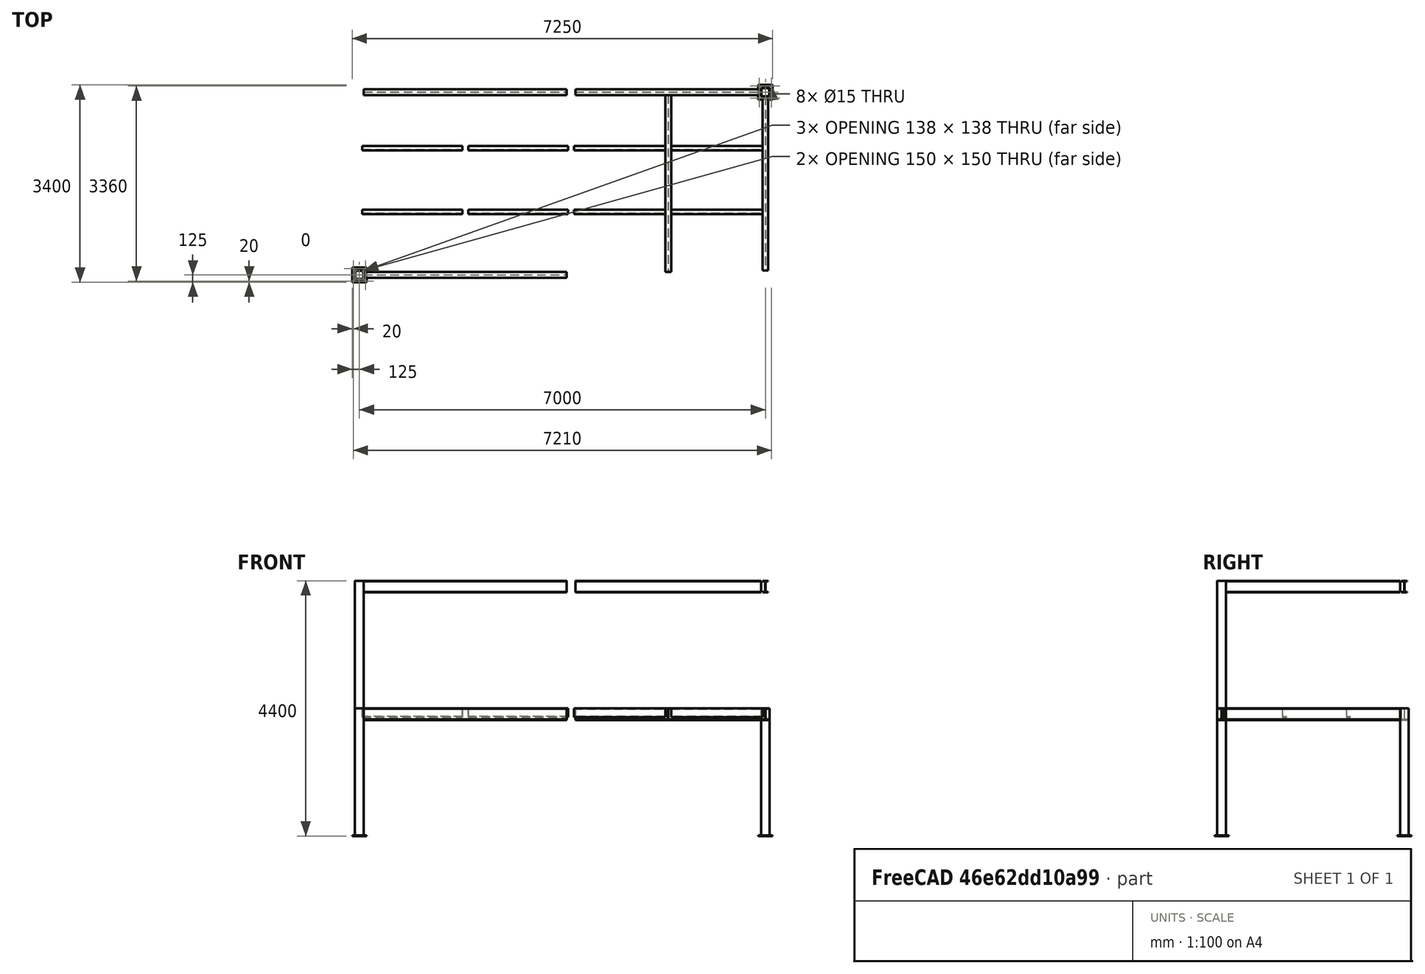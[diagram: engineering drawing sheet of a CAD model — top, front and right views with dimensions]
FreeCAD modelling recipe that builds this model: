
FCSTD DOCUMENT  (FreeCAD 0.20R29177 +426 (Git))
Label: steelframe2
License: All rights reserved
LicenseURL: http://en.wikipedia.org/wiki/All_rights_reserved
objects: App::FeaturePython×181, Part::FeaturePython×121, App::Link×12, Part::Extrusion×1, Part::MultiFuse×1
note: 122 computed .brp shape members not serialized (recipe doc carries the construction recipe); baked Part::Feature solids carry a one-line shape summary decoded from their .brp

FEATURE [Part::FeaturePython] BasePlate  # WARN: FeaturePython — macro-defined, semantics opaque (R4)
  B = 250
  D = 15
  H = 250
  b1 = 20
  h1 = 20
  sface = 0
FEATURE [Part::FeaturePython] SquarePipe_SS  # WARN: FeaturePython — macro-defined, semantics opaque (R4)
  L = 2200
  Solid = true
  size = 43
  standard = SS
FEATURE [Part::Extrusion] Extrude
  Base = -> BasePlate
  Dir = (0,0,1)
  DirMode = 2
  FaceMakerClass = Part::FaceMakerBullseye
  LengthFwd = 9
  LengthRev = 0
  Solid = true
  Symmetric = false
FEATURE [Part::MultiFuse] Fusion  label="Square-steel pipe"
  Placement = pos=(1.063e-12,6.983e-12,237) rot=(0,0,1;0rad)
  Shapes = -> [SquarePipe_SS,Extrude]
FEATURE [Part::FeaturePython] H200x100x5_5_8  label="H_thin"  # WARN: FeaturePython — macro-defined, semantics opaque (R4)
  L = 3000
  Placement = pos=(1.1069e-12,3075,2337) rot=(1,0,0;1.5708rad)
  Solid = true
  size = 5
  standard = SS_Thin
FEATURE [App::Link] Link  label="Square-steel pipe001"
  LinkPlacement = pos=(3650,2.14375e-11,237) rot=(0,0,1;0rad)
  LinkedObject = -> Fusion
  Placement = pos=(3650,2.14375e-11,237) rot=(0,0,1;0rad)
FEATURE [Part::FeaturePython] H200x100x5_5_009  label="H_thin001"  # WARN: FeaturePython — macro-defined, semantics opaque (R4)
  L = 3500
  Placement = pos=(75,7.6577e-12,2337) rot=(0.57735,0.57735,0.57735;2.0944rad)
  Solid = true
  size = 5
  standard = SS_Thin
  expr: L = 3500
FEATURE [App::Link] Link001  label="Square-steel pipe002"
  LinkPlacement = pos=(1.0657e-12,3150,237) rot=(0,0,1;0rad)
  LinkedObject = -> Fusion
  Placement = pos=(1.0657e-12,3150,237) rot=(0,0,1;0rad)
FEATURE [Part::FeaturePython] H200x100x5_5_010  label="H_thin002"  # WARN: FeaturePython — macro-defined, semantics opaque (R4)
  L = 3200
  Placement = pos=(3725,-3.5035e-12,2337) rot=(0.57735,0.57735,0.57735;2.0944rad)
  Solid = true
  size = 5
  standard = SS_Thin
FEATURE [App::Link] Link002  label="Square-steel pipe003"
  LinkPlacement = pos=(7000,-1.45687e-10,237) rot=(0,0,1;0rad)
  LinkedObject = -> Link
  Placement = pos=(7000,-1.45687e-10,237) rot=(0,0,1;0rad)
FEATURE [App::Link] Link003  label="H_thin003"
  LinkPlacement = pos=(75,3150,2337) rot=(0.57735,0.57735,0.57735;2.0944rad)
  LinkedObject = -> H200x100x5_5_009
  Placement = pos=(75,3150,2337) rot=(0.57735,0.57735,0.57735;2.0944rad)
FEATURE [App::Link] Link004  label="Square-steel pipe004"
  LinkPlacement = pos=(3650,3150,237) rot=(0,0,1;0rad)
  LinkedObject = -> Link
  Placement = pos=(3650,3150,237) rot=(0,0,1;0rad)
FEATURE [Part::FeaturePython] Clone  label="H_thin004"  # Draft clone (typed FeaturePython)
  AttacherType = Attacher::AttachEngine3D
  Fuse = false
  Objects = -> [H200x100x5_5_8]
  Placement = pos=(3650,3075,2337) rot=(1,0,0;1.5708rad)
  Scale = (1,1,1)
FEATURE [Part::FeaturePython] Clone001  label="H_thin005"  # Draft clone (typed FeaturePython)
  AttacherType = Attacher::AttachEngine3D
  Fuse = false
  Objects = -> [H200x100x5_5_010]
  Placement = pos=(3725,3150,2337) rot=(0.57735,0.57735,0.57735;2.0944rad)
  Scale = (1,1,1)
FEATURE [Part::FeaturePython] Clone002  label="Square-steel pipe005"  # Draft clone (typed FeaturePython)
  AttacherType = Attacher::AttachEngine3D
  Fuse = false
  Objects = -> [Link002]
  Placement = pos=(7000,3150,237) rot=(0,0,1;0rad)
  Scale = (1,1,1)
FEATURE [Part::FeaturePython] Clone003  label="H_thin006"  # Draft clone (typed FeaturePython)
  AttacherType = Attacher::AttachEngine3D
  Fuse = false
  Objects = -> [Clone]
  Placement = pos=(7000,3075,2337) rot=(1,0,0;1.5708rad)
  Scale = (1,1,1)
FEATURE [Part::FeaturePython] H200x100x5_5_011  label="H_thin007"  # WARN: FeaturePython — macro-defined, semantics opaque (R4)
  L = 3050
  Placement = pos=(1825,3100,2337) rot=(1,0,0;1.5708rad)
  Solid = true
  size = 5
  standard = SS_Thin
FEATURE [Part::FeaturePython] Clone004  label="H_thin008"  # Draft clone (typed FeaturePython)
  AttacherType = Attacher::AttachEngine3D
  Fuse = false
  Objects = -> [H200x100x5_5_011]
  Placement = pos=(5325,3100,2337) rot=(1,0,0;1.5708rad)
  Scale = (1,1,1)
FEATURE [Part::FeaturePython] C150x75x007  label="Channel001"  # WARN: FeaturePython — macro-defined, semantics opaque (R4)
  L = 1575
  Placement = pos=(3700,1086.25,2362) rot=(0.57735,0.57735,0.57735;2.0944rad)
  Solid = true
  size = 3
  standard = SS
FEATURE [Part::FeaturePython] C150x75x008  label="Channel002"  # WARN: FeaturePython — macro-defined, semantics opaque (R4)
  L = 1725
  Placement = pos=(50.0219,1086.25,2362) rot=(0.57735,0.57735,0.57735;2.0944rad)
  Solid = true
  size = 3
  standard = SS
FEATURE [Part::FeaturePython] SquarePipe_SS001  label="SQ_Pipe"  # WARN: FeaturePython — macro-defined, semantics opaque (R4)
  L = 2200
  Placement = pos=(1.063e-12,2.583e-12,2437) rot=(0,0,1;2e-06rad)
  Solid = true
  size = 43
  standard = SS
FEATURE [App::Link] Link005  label="SQ_Pipe001"
  LinkPlacement = pos=(1.0817e-12,3150,2437) rot=(0,0,1;0rad)
  LinkedObject = -> SquarePipe_SS001
  Placement = pos=(1.0817e-12,3150,2437) rot=(0,0,1;0rad)
FEATURE [App::Link] Link006  label="SQ_Pipe002"
  LinkPlacement = pos=(3650,-1.32887e-11,2437) rot=(0,0,1;0rad)
  LinkedObject = -> SquarePipe_SS001
  Placement = pos=(3650,-1.32887e-11,2437) rot=(0,0,1;0rad)
FEATURE [App::Link] Link007  label="SQ_Pipe003"
  LinkPlacement = pos=(3650,3150,2437) rot=(0,0,1;0rad)
  LinkedObject = -> Link006
  Placement = pos=(3650,3150,2437) rot=(0,0,1;0rad)
FEATURE [App::Link] Link008  label="SQ_Pipe004"
  LinkPlacement = pos=(7000,2.22996e-10,2437) rot=(0,0,1;0rad)
  LinkedObject = -> Link007
  Placement = pos=(7000,2.22996e-10,2437) rot=(0,0,1;0rad)
FEATURE [App::Link] Link009  label="SQ_Pipe005"
  LinkPlacement = pos=(7000,3150,2437) rot=(0,0,1;0rad)
  LinkedObject = -> Link008
  Placement = pos=(7000,3150,2437) rot=(0,0,1;0rad)
FEATURE [App::Link] Link010  label="H_thin009"
  LinkPlacement = pos=(75,0.000150522,4537) rot=(0.577351,-0.57735,0.57735;4.18879rad)
  LinkedObject = -> H200x100x5_5_009
  Placement = pos=(75,0.000150522,4537) rot=(0.577351,-0.57735,0.57735;4.18879rad)
FEATURE [App::Link] Link011  label="H_thin010"
  LinkPlacement = pos=(-0.000150522,75,4537) rot=(-1,-1e-06,1e-06;1.5708rad)
  LinkedObject = -> H200x100x5_5_8
  Placement = pos=(-0.000150522,75,4537) rot=(-1,-1e-06,1e-06;1.5708rad)
FEATURE [Part::FeaturePython] Clone005  label="H_thin011"  # Draft clone (typed FeaturePython)
  AttacherType = Attacher::AttachEngine3D
  Fuse = false
  Objects = -> [H200x100x5_5_010]
  Placement = pos=(3725,-1.20515e-10,4537) rot=(0.57735,0.57735,0.57735;2.0944rad)
  Scale = (1,1,1)
FEATURE [Part::FeaturePython] Clone006  label="H_thin012"  # Draft clone (typed FeaturePython)
  AttacherType = Attacher::AttachEngine3D
  Fuse = false
  Objects = -> [Link011]
  Placement = pos=(3650,75,4537) rot=(-1,0,0;1.5708rad)
  Scale = (1,1,1)
FEATURE [Part::FeaturePython] Clone007  label="H_thin013"  # Draft clone (typed FeaturePython)
  AttacherType = Attacher::AttachEngine3D
  Fuse = false
  Objects = -> [Clone006]
  Placement = pos=(7000,75,4537) rot=(-1,0,0;1.5708rad)
  Scale = (1,1,1)
FEATURE [Part::FeaturePython] Clone008  label="H_thin014"  # Draft clone (typed FeaturePython)
  AttacherType = Attacher::AttachEngine3D
  Fuse = false
  Objects = -> [Link010]
  Placement = pos=(75,3150,4537) rot=(-0.57735,0.57735,-0.57735;2.0944rad)
  Scale = (1,1,1)
FEATURE [Part::FeaturePython] Clone009  label="H_thin015"  # Draft clone (typed FeaturePython)
  AttacherType = Attacher::AttachEngine3D
  Fuse = false
  Objects = -> [Clone005]
  Placement = pos=(3725,3150,4537) rot=(0.57735,0.57735,0.57735;2.0944rad)
  Scale = (1,1,1)
FEATURE [Part::FeaturePython] Array002  # Draft array (typed FeaturePython)
  Angle = 360
  ArrayType = 0
  Axis = (0,0,1)
  Base = -> C150x75x007
  Center = (0,0,0)
  Fuse = false
  IntervalAxis = (0,0,0)
  IntervalX = (1675,0,0)
  IntervalY = (0,1100,0)
  IntervalZ = (0,0,50)
  NumberCircles = 3
  NumberPolar = 5
  NumberX = 2
  NumberY = 2
  NumberZ = 1
  RadialDistance = 50
  Symmetry = 1
  TangentialDistance = 25
FEATURE [Part::FeaturePython] Array  # Draft array (typed FeaturePython)
  Angle = 360
  ArrayType = 0
  Axis = (0,0,1)
  Base = -> C150x75x008
  Center = (0,0,0)
  Fuse = false
  IntervalAxis = (0,0,0)
  IntervalX = (1826,0,0)
  IntervalY = (0,1100,0)
  IntervalZ = (0,0,50)
  NumberCircles = 3
  NumberPolar = 5
  NumberX = 2
  NumberY = 2
  NumberZ = 1
  RadialDistance = 50
  Symmetry = 1
  TangentialDistance = 25
FEATURE [Part::FeaturePython] Parts  # WARN: FeaturePython — macro-defined, semantics opaque (R4)
  Group = -> [Fusion,H200x100x5_5_8,Link,H200x100x5_5_009,Link001,H200x100x5_5_010,Link002,Link003,Link004,Clone,Clone001,Clone002,Clone003,H200x100x5_5_011,Clone004,C150x75x007,C150x75x008,SquarePipe_SS001,Link005,Link006,Link007,Link008,Link009,Link010,Link011,Clone005,Clone006,Clone007,Clone008,Clone009,Array002,Array]
  GroupMode = 0
FEATURE [Part::FeaturePython] Assembly  # WARN: FeaturePython — macro-defined, semantics opaque (R4)
  AutoRelax = true
  BuildShape = 0
  Freeze = false
  Group = -> [Constraints,Elements,Parts]
  Verbose = false
  _SolverType = 1
  _Version = 1
FEATURE [App::FeaturePython] Constraints  # WARN: FeaturePython — macro-defined, semantics opaque (R4)
  Group = -> [Constraint,Constraint001,Constraint002,Constraint003,Constraint004,Constraint005,Constraint006,Constraint007,Constraint008,Constraint009,Constraint010,Constraint011,Constraint012,Constraint013,Constraint014,Constraint015,Constraint016,Constraint017,Constraint018,Constraint019,Constraint020,Constraint021,Constraint022,Constraint023,Constraint024,Constraint025,Constraint026,Constraint027,+32 more]
  _Version = 1
FEATURE [App::FeaturePython] Elements  # WARN: FeaturePython — macro-defined, semantics opaque (R4)
  Group = -> [_Element,_Element001,_Element002,_Element003,_Element004,_Element005,_Element006,_Element007,_Element008,_Element009,_Element010,_Element011,_Element012,_Element013,_Element014,_Element015,_Element016,_Element017,_Element018,_Element019,_Element020,_Element021,_Element022,_Element023,_Element024,_Element025,_Element026,_Element027,_Element028,_Element029,_Element030,_Element031,_Element032,+65 more]
FEATURE [App::FeaturePython] Constraint  label="PlaneCoincident"  # WARN: FeaturePython — macro-defined, semantics opaque (R4)
  Angle = 0
  AnglePitch = 0
  AngleRoll = 0
  Cascade = false
  Disabled = false
  Group = -> [ElementLink,ElementLink001]
  LockAngle = false
  Multiply = false
  OffsetX = 0
  OffsetY = 0
  _ConstraintType = 35
  _Parent = -> Constraints
FEATURE [App::FeaturePython] ElementLink  label="_Element"  # link proxy (typed FeaturePython)
  LinkTransform = true
  LinkedObject = -> _Element
  _Parent = -> Constraint
FEATURE [Part::FeaturePython] _Element  # link proxy (typed FeaturePython)
  Detach = false
  LinkTransform = true
  LinkedObject = -> SquarePipe_SS001 [Face17]
  _Parent = -> Elements
FEATURE [App::FeaturePython] ElementLink001  label="_Element001"  # link proxy (typed FeaturePython)
  LinkTransform = true
  LinkedObject = -> _Element001
  _Parent = -> Constraint
FEATURE [Part::FeaturePython] _Element001  # link proxy (typed FeaturePython)
  Detach = false
  LinkTransform = true
  LinkedObject = -> Fusion [Face21]
  _Parent = -> Elements
FEATURE [Part::FeaturePython] _Element002  # link proxy (typed FeaturePython)
  Detach = false
  LinkTransform = true
  LinkedObject = -> H200x100x5_5_009 [Edge47]
  _Parent = -> Elements
FEATURE [Part::FeaturePython] _Element003  # link proxy (typed FeaturePython)
  Detach = false
  LinkTransform = true
  LinkedObject = -> Fusion [Edge59]
  _Parent = -> Elements
FEATURE [App::FeaturePython] Constraint001  label="Locked"  # WARN: FeaturePython — macro-defined, semantics opaque (R4)
  Disabled = false
  Group = -> [ElementLink002]
  _ConstraintType = 0
  _Parent = -> Constraints
FEATURE [App::FeaturePython] ElementLink002  label="_Element004"  # link proxy (typed FeaturePython)
  LinkTransform = true
  LinkedObject = -> _Element004
  _Parent = -> Constraint001
FEATURE [Part::FeaturePython] _Element004  # link proxy (typed FeaturePython)
  Detach = false
  LinkTransform = true
  LinkedObject = -> Fusion [Face16]
  _Parent = -> Elements
FEATURE [App::FeaturePython] Constraint002  label="MidPoint"  # WARN: FeaturePython — macro-defined, semantics opaque (R4)
  Disabled = false
  Group = -> [ElementLink003,ElementLink004]
  _ConstraintType = 20
  _Parent = -> Constraints
FEATURE [App::FeaturePython] ElementLink003  label="_Element002"  # link proxy (typed FeaturePython)
  LinkTransform = true
  LinkedObject = -> _Element002
  _Parent = -> Constraint002
FEATURE [App::FeaturePython] ElementLink004  label="_Element003"  # link proxy (typed FeaturePython)
  LinkTransform = true
  LinkedObject = -> _Element003
  _Parent = -> Constraint002
FEATURE [Part::FeaturePython] _Element005  # link proxy (typed FeaturePython)
  Detach = false
  LinkTransform = true
  LinkedObject = -> H200x100x5_5_009 [Vertex15]
  _Parent = -> Elements
FEATURE [App::FeaturePython] Constraint003  label="PlaneAlignment"  # WARN: FeaturePython — macro-defined, semantics opaque (R4)
  Angle = 0
  AnglePitch = 0
  AngleRoll = 0
  Cascade = false
  Disabled = false
  Group = -> [ElementLink005,ElementLink006]
  LockAngle = false
  _ConstraintType = 37
  _Parent = -> Constraints
FEATURE [App::FeaturePython] ElementLink005  label="_Element006"  # link proxy (typed FeaturePython)
  LinkTransform = true
  LinkedObject = -> _Element006
  _Parent = -> Constraint003
FEATURE [Part::FeaturePython] _Element006  # link proxy (typed FeaturePython)
  Detach = false
  LinkTransform = true
  LinkedObject = -> H200x100x5_5_009 [Face16]
  _Parent = -> Elements
FEATURE [App::FeaturePython] ElementLink006  label="_Element001"  # link proxy (typed FeaturePython)
  LinkTransform = true
  LinkedObject = -> _Element001
  _Parent = -> Constraint003
FEATURE [App::FeaturePython] Constraint004  label="SameOrientation"  # WARN: FeaturePython — macro-defined, semantics opaque (R4)
  Disabled = false
  Group = -> [ElementLink007,ElementLink008]
  _ConstraintType = 2
  _Parent = -> Constraints
FEATURE [App::FeaturePython] ElementLink007  label="_Element006"  # link proxy (typed FeaturePython)
  LinkTransform = true
  LinkedObject = -> _Element006
  _Parent = -> Constraint004
FEATURE [App::FeaturePython] ElementLink008  label="_Element001"  # link proxy (typed FeaturePython)
  LinkTransform = true
  LinkedObject = -> _Element001
  _Parent = -> Constraint004
FEATURE [App::FeaturePython] Constraint005  label="MidPoint001"  # WARN: FeaturePython — macro-defined, semantics opaque (R4)
  Disabled = false
  Group = -> [ElementLink009,ElementLink010]
  _ConstraintType = 20
  _Parent = -> Constraints
FEATURE [App::FeaturePython] ElementLink009  label="_Element007"  # link proxy (typed FeaturePython)
  LinkTransform = true
  LinkedObject = -> _Element007
  _Parent = -> Constraint005
FEATURE [Part::FeaturePython] _Element007  # link proxy (typed FeaturePython)
  Detach = false
  LinkTransform = true
  LinkedObject = -> H200x100x5_5_009 [Edge48]
  _Parent = -> Elements
FEATURE [App::FeaturePython] ElementLink010  label="_Element008"  # link proxy (typed FeaturePython)
  LinkTransform = true
  LinkedObject = -> _Element008
  _Parent = -> Constraint005
FEATURE [Part::FeaturePython] _Element008  # link proxy (typed FeaturePython)
  Detach = false
  LinkTransform = true
  LinkedObject = -> Link [Edge50]
  _Parent = -> Elements
FEATURE [App::FeaturePython] Constraint006  label="SameOrientation001"  # WARN: FeaturePython — macro-defined, semantics opaque (R4)
  Disabled = false
  Group = -> [ElementLink011,ElementLink012]
  _ConstraintType = 2
  _Parent = -> Constraints
FEATURE [App::FeaturePython] ElementLink011  label="_Element006"  # link proxy (typed FeaturePython)
  LinkTransform = true
  LinkedObject = -> _Element006
  _Parent = -> Constraint006
FEATURE [App::FeaturePython] ElementLink012  label="_Element009"  # link proxy (typed FeaturePython)
  LinkTransform = true
  LinkedObject = -> _Element009
  _Parent = -> Constraint006
FEATURE [Part::FeaturePython] _Element009  # link proxy (typed FeaturePython)
  Detach = false
  LinkTransform = true
  LinkedObject = -> Link [Face21]
  _Parent = -> Elements
FEATURE [App::FeaturePython] Constraint007  label="MidPoint002"  # WARN: FeaturePython — macro-defined, semantics opaque (R4)
  Disabled = false
  Group = -> [ElementLink013,ElementLink014]
  _ConstraintType = 20
  _Parent = -> Constraints
FEATURE [App::FeaturePython] ElementLink013  label="_Element010"  # link proxy (typed FeaturePython)
  LinkTransform = true
  LinkedObject = -> _Element010
  _Parent = -> Constraint007
FEATURE [Part::FeaturePython] _Element010  # link proxy (typed FeaturePython)
  Detach = false
  LinkTransform = true
  LinkedObject = -> Link006 [Edge18]
  _Parent = -> Elements
FEATURE [App::FeaturePython] ElementLink014  label="_Element011"  # link proxy (typed FeaturePython)
  LinkTransform = true
  LinkedObject = -> _Element011
  _Parent = -> Constraint007
FEATURE [Part::FeaturePython] _Element011  # link proxy (typed FeaturePython)
  Detach = false
  LinkTransform = true
  LinkedObject = -> Link [Edge55]
  _Parent = -> Elements
FEATURE [App::FeaturePython] Constraint008  label="SameOrientation002"  # WARN: FeaturePython — macro-defined, semantics opaque (R4)
  Disabled = false
  Group = -> [ElementLink015,ElementLink016]
  _ConstraintType = 2
  _Parent = -> Constraints
FEATURE [App::FeaturePython] ElementLink015  label="_Element012"  # link proxy (typed FeaturePython)
  LinkTransform = true
  LinkedObject = -> _Element012
  _Parent = -> Constraint008
FEATURE [Part::FeaturePython] _Element012  # link proxy (typed FeaturePython)
  Detach = false
  LinkTransform = true
  LinkedObject = -> Link006 [Face6]
  _Parent = -> Elements
FEATURE [App::FeaturePython] ElementLink016  label="_Element013"  # link proxy (typed FeaturePython)
  LinkTransform = true
  LinkedObject = -> _Element013
  _Parent = -> Constraint008
FEATURE [Part::FeaturePython] _Element013  # link proxy (typed FeaturePython)
  Detach = false
  LinkTransform = true
  LinkedObject = -> Link [Face14]
  _Parent = -> Elements
FEATURE [App::FeaturePython] Constraint009  label="MidPoint003"  # WARN: FeaturePython — macro-defined, semantics opaque (R4)
  Disabled = false
  Group = -> [ElementLink017,ElementLink018]
  _ConstraintType = 20
  _Parent = -> Constraints
FEATURE [App::FeaturePython] ElementLink017  label="_Element014"  # link proxy (typed FeaturePython)
  LinkTransform = true
  LinkedObject = -> _Element014
  _Parent = -> Constraint009
FEATURE [Part::FeaturePython] _Element014  # link proxy (typed FeaturePython)
  Detach = false
  LinkTransform = true
  LinkedObject = -> H200x100x5_5_010 [Edge47]
  _Parent = -> Elements
FEATURE [App::FeaturePython] ElementLink018  label="_Element015"  # link proxy (typed FeaturePython)
  LinkTransform = true
  LinkedObject = -> _Element015
  _Parent = -> Constraint009
FEATURE [Part::FeaturePython] _Element015  # link proxy (typed FeaturePython)
  Detach = false
  LinkTransform = true
  LinkedObject = -> Link006 [Edge12]
  _Parent = -> Elements
FEATURE [App::FeaturePython] Constraint010  label="SameOrientation003"  # WARN: FeaturePython — macro-defined, semantics opaque (R4)
  Disabled = false
  Group = -> [ElementLink019,ElementLink020]
  _ConstraintType = 2
  _Parent = -> Constraints
FEATURE [App::FeaturePython] ElementLink019  label="_Element016"  # link proxy (typed FeaturePython)
  LinkTransform = true
  LinkedObject = -> _Element016
  _Parent = -> Constraint010
FEATURE [Part::FeaturePython] _Element016  # link proxy (typed FeaturePython)
  Detach = false
  LinkTransform = true
  LinkedObject = -> H200x100x5_5_010 [Face16]
  _Parent = -> Elements
FEATURE [App::FeaturePython] ElementLink020  label="_Element009"  # link proxy (typed FeaturePython)
  LinkTransform = true
  LinkedObject = -> _Element009
  _Parent = -> Constraint010
FEATURE [App::FeaturePython] Constraint011  label="MidPoint004"  # WARN: FeaturePython — macro-defined, semantics opaque (R4)
  Disabled = false
  Group = -> [ElementLink021,ElementLink022]
  _ConstraintType = 20
  _Parent = -> Constraints
FEATURE [App::FeaturePython] ElementLink021  label="_Element017"  # link proxy (typed FeaturePython)
  LinkTransform = true
  LinkedObject = -> _Element017
  _Parent = -> Constraint011
FEATURE [Part::FeaturePython] _Element017  # link proxy (typed FeaturePython)
  Detach = false
  LinkTransform = true
  LinkedObject = -> Link002 [Edge50]
  _Parent = -> Elements
FEATURE [App::FeaturePython] ElementLink022  label="_Element018"  # link proxy (typed FeaturePython)
  LinkTransform = true
  LinkedObject = -> _Element018
  _Parent = -> Constraint011
FEATURE [Part::FeaturePython] _Element018  # link proxy (typed FeaturePython)
  Detach = false
  LinkTransform = true
  LinkedObject = -> H200x100x5_5_010 [Edge48]
  _Parent = -> Elements
FEATURE [App::FeaturePython] Constraint012  label="SameOrientation004"  # WARN: FeaturePython — macro-defined, semantics opaque (R4)
  Disabled = false
  Group = -> [ElementLink023,ElementLink024]
  _ConstraintType = 2
  _Parent = -> Constraints
FEATURE [App::FeaturePython] ElementLink023  label="_Element016"  # link proxy (typed FeaturePython)
  LinkTransform = true
  LinkedObject = -> _Element016
  _Parent = -> Constraint012
FEATURE [App::FeaturePython] ElementLink024  label="_Element019"  # link proxy (typed FeaturePython)
  LinkTransform = true
  LinkedObject = -> _Element019
  _Parent = -> Constraint012
FEATURE [Part::FeaturePython] _Element019  # link proxy (typed FeaturePython)
  Detach = false
  LinkTransform = true
  LinkedObject = -> Link002 [Face21]
  _Parent = -> Elements
FEATURE [App::FeaturePython] Constraint013  label="MidPoint005"  # WARN: FeaturePython — macro-defined, semantics opaque (R4)
  Disabled = false
  Group = -> [ElementLink025,ElementLink026]
  _ConstraintType = 20
  _Parent = -> Constraints
FEATURE [App::FeaturePython] ElementLink025  label="_Element020"  # link proxy (typed FeaturePython)
  LinkTransform = true
  LinkedObject = -> _Element020
  _Parent = -> Constraint013
FEATURE [Part::FeaturePython] _Element020  # link proxy (typed FeaturePython)
  Detach = false
  LinkTransform = true
  LinkedObject = -> Link008 [Edge18]
  _Parent = -> Elements
FEATURE [App::FeaturePython] ElementLink026  label="_Element021"  # link proxy (typed FeaturePython)
  LinkTransform = true
  LinkedObject = -> _Element021
  _Parent = -> Constraint013
FEATURE [Part::FeaturePython] _Element021  # link proxy (typed FeaturePython)
  Detach = false
  LinkTransform = true
  LinkedObject = -> Link002 [Edge55]
  _Parent = -> Elements
FEATURE [App::FeaturePython] Constraint014  label="SameOrientation005"  # WARN: FeaturePython — macro-defined, semantics opaque (R4)
  Disabled = false
  Group = -> [ElementLink027,ElementLink028]
  _ConstraintType = 2
  _Parent = -> Constraints
FEATURE [App::FeaturePython] ElementLink027  label="_Element022"  # link proxy (typed FeaturePython)
  LinkTransform = true
  LinkedObject = -> _Element022
  _Parent = -> Constraint014
FEATURE [Part::FeaturePython] _Element022  # link proxy (typed FeaturePython)
  Detach = false
  LinkTransform = true
  LinkedObject = -> Link008 [Face6]
  _Parent = -> Elements
FEATURE [App::FeaturePython] ElementLink028  label="_Element023"  # link proxy (typed FeaturePython)
  LinkTransform = true
  LinkedObject = -> _Element023
  _Parent = -> Constraint014
FEATURE [Part::FeaturePython] _Element023  # link proxy (typed FeaturePython)
  Detach = false
  LinkTransform = true
  LinkedObject = -> Link002 [Face14]
  _Parent = -> Elements
FEATURE [App::FeaturePython] Constraint015  label="MidPoint006"  # WARN: FeaturePython — macro-defined, semantics opaque (R4)
  Disabled = false
  Group = -> [ElementLink029,ElementLink030]
  _ConstraintType = 20
  _Parent = -> Constraints
FEATURE [App::FeaturePython] ElementLink029  label="_Element024"  # link proxy (typed FeaturePython)
  LinkTransform = true
  LinkedObject = -> _Element024
  _Parent = -> Constraint015
FEATURE [Part::FeaturePython] _Element024  # link proxy (typed FeaturePython)
  Detach = false
  LinkTransform = true
  LinkedObject = -> H200x100x5_5_8 [Edge48]
  _Parent = -> Elements
FEATURE [App::FeaturePython] ElementLink030  label="_Element025"  # link proxy (typed FeaturePython)
  LinkTransform = true
  LinkedObject = -> _Element025
  _Parent = -> Constraint015
FEATURE [Part::FeaturePython] _Element025  # link proxy (typed FeaturePython)
  Detach = false
  LinkTransform = true
  LinkedObject = -> Fusion [Edge63]
  _Parent = -> Elements
FEATURE [App::FeaturePython] Constraint016  label="SameOrientation006"  # WARN: FeaturePython — macro-defined, semantics opaque (R4)
  Disabled = false
  Group = -> [ElementLink031,ElementLink032]
  _ConstraintType = 2
  _Parent = -> Constraints
FEATURE [App::FeaturePython] ElementLink031  label="_Element026"  # link proxy (typed FeaturePython)
  LinkTransform = true
  LinkedObject = -> _Element026
  _Parent = -> Constraint016
FEATURE [Part::FeaturePython] _Element026  # link proxy (typed FeaturePython)
  Detach = false
  LinkTransform = true
  LinkedObject = -> H200x100x5_5_8 [Face16]
  _Parent = -> Elements
FEATURE [App::FeaturePython] ElementLink032  label="_Element001"  # link proxy (typed FeaturePython)
  LinkTransform = true
  LinkedObject = -> _Element001
  _Parent = -> Constraint016
FEATURE [App::FeaturePython] Constraint017  label="MidPoint007"  # WARN: FeaturePython — macro-defined, semantics opaque (R4)
  Disabled = false
  Group = -> [ElementLink033,ElementLink034]
  _ConstraintType = 20
  _Parent = -> Constraints
FEATURE [App::FeaturePython] ElementLink033  label="_Element027"  # link proxy (typed FeaturePython)
  LinkTransform = true
  LinkedObject = -> _Element027
  _Parent = -> Constraint017
FEATURE [Part::FeaturePython] _Element027  # link proxy (typed FeaturePython)
  Detach = false
  LinkTransform = true
  LinkedObject = -> Clone [Edge48]
  _Parent = -> Elements
FEATURE [App::FeaturePython] ElementLink034  label="_Element028"  # link proxy (typed FeaturePython)
  LinkTransform = true
  LinkedObject = -> _Element028
  _Parent = -> Constraint017
FEATURE [Part::FeaturePython] _Element028  # link proxy (typed FeaturePython)
  Detach = false
  LinkTransform = true
  LinkedObject = -> Link [Edge63]
  _Parent = -> Elements
FEATURE [App::FeaturePython] Constraint018  label="SameOrientation007"  # WARN: FeaturePython — macro-defined, semantics opaque (R4)
  Disabled = false
  Group = -> [ElementLink035,ElementLink036]
  _ConstraintType = 2
  _Parent = -> Constraints
FEATURE [App::FeaturePython] ElementLink035  label="_Element029"  # link proxy (typed FeaturePython)
  LinkTransform = true
  LinkedObject = -> _Element029
  _Parent = -> Constraint018
FEATURE [Part::FeaturePython] _Element029  # link proxy (typed FeaturePython)
  Detach = false
  LinkTransform = true
  LinkedObject = -> Clone [Face16]
  _Parent = -> Elements
FEATURE [App::FeaturePython] ElementLink036  label="_Element009"  # link proxy (typed FeaturePython)
  LinkTransform = true
  LinkedObject = -> _Element009
  _Parent = -> Constraint018
FEATURE [App::FeaturePython] Constraint019  label="MidPoint008"  # WARN: FeaturePython — macro-defined, semantics opaque (R4)
  Disabled = false
  Group = -> [ElementLink037,ElementLink038]
  _ConstraintType = 20
  _Parent = -> Constraints
FEATURE [App::FeaturePython] ElementLink037  label="_Element030"  # link proxy (typed FeaturePython)
  LinkTransform = true
  LinkedObject = -> _Element030
  _Parent = -> Constraint019
FEATURE [Part::FeaturePython] _Element030  # link proxy (typed FeaturePython)
  Detach = false
  LinkTransform = true
  LinkedObject = -> Clone003 [Edge48]
  _Parent = -> Elements
FEATURE [App::FeaturePython] ElementLink038  label="_Element031"  # link proxy (typed FeaturePython)
  LinkTransform = true
  LinkedObject = -> _Element031
  _Parent = -> Constraint019
FEATURE [Part::FeaturePython] _Element031  # link proxy (typed FeaturePython)
  Detach = false
  LinkTransform = true
  LinkedObject = -> Link002 [Edge63]
  _Parent = -> Elements
FEATURE [App::FeaturePython] Constraint020  label="SameOrientation008"  # WARN: FeaturePython — macro-defined, semantics opaque (R4)
  Disabled = false
  Group = -> [ElementLink039,ElementLink040]
  _ConstraintType = 2
  _Parent = -> Constraints
FEATURE [App::FeaturePython] ElementLink039  label="_Element032"  # link proxy (typed FeaturePython)
  LinkTransform = true
  LinkedObject = -> _Element032
  _Parent = -> Constraint020
FEATURE [Part::FeaturePython] _Element032  # link proxy (typed FeaturePython)
  Detach = false
  LinkTransform = true
  LinkedObject = -> Clone003 [Face16]
  _Parent = -> Elements
FEATURE [App::FeaturePython] ElementLink040  label="_Element019"  # link proxy (typed FeaturePython)
  LinkTransform = true
  LinkedObject = -> _Element019
  _Parent = -> Constraint020
FEATURE [App::FeaturePython] Constraint021  label="MidPoint009"  # WARN: FeaturePython — macro-defined, semantics opaque (R4)
  Disabled = false
  Group = -> [ElementLink041,ElementLink042]
  _ConstraintType = 20
  _Parent = -> Constraints
FEATURE [App::FeaturePython] ElementLink041  label="_Element033"  # link proxy (typed FeaturePython)
  LinkTransform = true
  LinkedObject = -> _Element033
  _Parent = -> Constraint021
FEATURE [Part::FeaturePython] _Element033  # link proxy (typed FeaturePython)
  Detach = false
  LinkTransform = true
  LinkedObject = -> Link001 [Edge55]
  _Parent = -> Elements
FEATURE [App::FeaturePython] ElementLink042  label="_Element034"  # link proxy (typed FeaturePython)
  LinkTransform = true
  LinkedObject = -> _Element034
  _Parent = -> Constraint021
FEATURE [Part::FeaturePython] _Element034  # link proxy (typed FeaturePython)
  Detach = false
  LinkTransform = true
  LinkedObject = -> H200x100x5_5_8 [Edge47]
  _Parent = -> Elements
FEATURE [App::FeaturePython] Constraint022  label="SameOrientation009"  # WARN: FeaturePython — macro-defined, semantics opaque (R4)
  Disabled = false
  Group = -> [ElementLink043,ElementLink044]
  _ConstraintType = 2
  _Parent = -> Constraints
FEATURE [App::FeaturePython] ElementLink043  label="_Element026"  # link proxy (typed FeaturePython)
  LinkTransform = true
  LinkedObject = -> _Element026
  _Parent = -> Constraint022
FEATURE [App::FeaturePython] ElementLink044  label="_Element035"  # link proxy (typed FeaturePython)
  LinkTransform = true
  LinkedObject = -> _Element035
  _Parent = -> Constraint022
FEATURE [Part::FeaturePython] _Element035  # link proxy (typed FeaturePython)
  Detach = false
  LinkTransform = true
  LinkedObject = -> Link001 [Face21]
  _Parent = -> Elements
FEATURE [App::FeaturePython] Constraint023  label="MidPoint010"  # WARN: FeaturePython — macro-defined, semantics opaque (R4)
  Disabled = false
  Group = -> [ElementLink045,ElementLink046]
  _ConstraintType = 20
  _Parent = -> Constraints
FEATURE [App::FeaturePython] ElementLink045  label="_Element036"  # link proxy (typed FeaturePython)
  LinkTransform = true
  LinkedObject = -> _Element036
  _Parent = -> Constraint023
FEATURE [Part::FeaturePython] _Element036  # link proxy (typed FeaturePython)
  Detach = false
  LinkTransform = true
  LinkedObject = -> Link005 [Edge12]
  _Parent = -> Elements
FEATURE [App::FeaturePython] ElementLink046  label="_Element037"  # link proxy (typed FeaturePython)
  LinkTransform = true
  LinkedObject = -> _Element037
  _Parent = -> Constraint023
FEATURE [Part::FeaturePython] _Element037  # link proxy (typed FeaturePython)
  Detach = false
  LinkTransform = true
  LinkedObject = -> Link001 [Edge59]
  _Parent = -> Elements
FEATURE [App::FeaturePython] Constraint024  label="SameOrientation010"  # WARN: FeaturePython — macro-defined, semantics opaque (R4)
  Disabled = false
  Group = -> [ElementLink047,ElementLink048]
  _ConstraintType = 2
  _Parent = -> Constraints
FEATURE [App::FeaturePython] ElementLink047  label="_Element038"  # link proxy (typed FeaturePython)
  LinkTransform = true
  LinkedObject = -> _Element038
  _Parent = -> Constraint024
FEATURE [Part::FeaturePython] _Element038  # link proxy (typed FeaturePython)
  Detach = false
  LinkTransform = true
  LinkedObject = -> Link001 [Face16]
  _Parent = -> Elements
FEATURE [App::FeaturePython] ElementLink048  label="_Element039"  # link proxy (typed FeaturePython)
  LinkTransform = true
  LinkedObject = -> _Element039
  _Parent = -> Constraint024
FEATURE [Part::FeaturePython] _Element039  # link proxy (typed FeaturePython)
  Detach = false
  LinkTransform = true
  LinkedObject = -> Link005 [Face4]
  _Parent = -> Elements
FEATURE [App::FeaturePython] Constraint025  label="MidPoint011"  # WARN: FeaturePython — macro-defined, semantics opaque (R4)
  Disabled = false
  Group = -> [ElementLink049,ElementLink050]
  _ConstraintType = 20
  _Parent = -> Constraints
FEATURE [App::FeaturePython] ElementLink049  label="_Element040"  # link proxy (typed FeaturePython)
  LinkTransform = true
  LinkedObject = -> _Element040
  _Parent = -> Constraint025
FEATURE [Part::FeaturePython] _Element040  # link proxy (typed FeaturePython)
  Detach = false
  LinkTransform = true
  LinkedObject = -> Clone [Edge47]
  _Parent = -> Elements
FEATURE [App::FeaturePython] ElementLink050  label="_Element041"  # link proxy (typed FeaturePython)
  LinkTransform = true
  LinkedObject = -> _Element041
  _Parent = -> Constraint025
FEATURE [Part::FeaturePython] _Element041  # link proxy (typed FeaturePython)
  Detach = false
  LinkTransform = true
  LinkedObject = -> Link004 [Edge55]
  _Parent = -> Elements
FEATURE [App::FeaturePython] Constraint026  label="SameOrientation011"  # WARN: FeaturePython — macro-defined, semantics opaque (R4)
  Disabled = false
  Group = -> [ElementLink051,ElementLink052]
  _ConstraintType = 2
  _Parent = -> Constraints
FEATURE [App::FeaturePython] ElementLink051  label="_Element029"  # link proxy (typed FeaturePython)
  LinkTransform = true
  LinkedObject = -> _Element029
  _Parent = -> Constraint026
FEATURE [App::FeaturePython] ElementLink052  label="_Element042"  # link proxy (typed FeaturePython)
  LinkTransform = true
  LinkedObject = -> _Element042
  _Parent = -> Constraint026
FEATURE [Part::FeaturePython] _Element042  # link proxy (typed FeaturePython)
  Detach = false
  LinkTransform = true
  LinkedObject = -> Link004 [Face21]
  _Parent = -> Elements
FEATURE [App::FeaturePython] Constraint027  label="MidPoint012"  # WARN: FeaturePython — macro-defined, semantics opaque (R4)
  Disabled = false
  Group = -> [ElementLink053,ElementLink054]
  _ConstraintType = 20
  _Parent = -> Constraints
FEATURE [App::FeaturePython] ElementLink053  label="_Element043"  # link proxy (typed FeaturePython)
  LinkTransform = true
  LinkedObject = -> _Element043
  _Parent = -> Constraint027
FEATURE [Part::FeaturePython] _Element043  # link proxy (typed FeaturePython)
  Detach = false
  LinkTransform = true
  LinkedObject = -> Link007 [Edge12]
  _Parent = -> Elements
FEATURE [App::FeaturePython] ElementLink054  label="_Element044"  # link proxy (typed FeaturePython)
  LinkTransform = true
  LinkedObject = -> _Element044
  _Parent = -> Constraint027
FEATURE [Part::FeaturePython] _Element044  # link proxy (typed FeaturePython)
  Detach = false
  LinkTransform = true
  LinkedObject = -> Link004 [Edge59]
  _Parent = -> Elements
FEATURE [App::FeaturePython] Constraint028  label="SameOrientation012"  # WARN: FeaturePython — macro-defined, semantics opaque (R4)
  Disabled = false
  Group = -> [ElementLink055,ElementLink056]
  _ConstraintType = 2
  _Parent = -> Constraints
FEATURE [App::FeaturePython] ElementLink055  label="_Element045"  # link proxy (typed FeaturePython)
  LinkTransform = true
  LinkedObject = -> _Element045
  _Parent = -> Constraint028
FEATURE [Part::FeaturePython] _Element045  # link proxy (typed FeaturePython)
  Detach = false
  LinkTransform = true
  LinkedObject = -> Link007 [Face4]
  _Parent = -> Elements
FEATURE [App::FeaturePython] ElementLink056  label="_Element046"  # link proxy (typed FeaturePython)
  LinkTransform = true
  LinkedObject = -> _Element046
  _Parent = -> Constraint028
FEATURE [Part::FeaturePython] _Element046  # link proxy (typed FeaturePython)
  Detach = false
  LinkTransform = true
  LinkedObject = -> Link004 [Face16]
  _Parent = -> Elements
FEATURE [App::FeaturePython] Constraint029  label="MidPoint013"  # WARN: FeaturePython — macro-defined, semantics opaque (R4)
  Disabled = false
  Group = -> [ElementLink057,ElementLink058]
  _ConstraintType = 20
  _Parent = -> Constraints
FEATURE [App::FeaturePython] ElementLink057  label="_Element047"  # link proxy (typed FeaturePython)
  LinkTransform = true
  LinkedObject = -> _Element047
  _Parent = -> Constraint029
FEATURE [Part::FeaturePython] _Element047  # link proxy (typed FeaturePython)
  Detach = false
  LinkTransform = true
  LinkedObject = -> Clone001 [Edge47]
  _Parent = -> Elements
FEATURE [App::FeaturePython] ElementLink058  label="_Element044"  # link proxy (typed FeaturePython)
  LinkTransform = true
  LinkedObject = -> _Element044
  _Parent = -> Constraint029
FEATURE [App::FeaturePython] Constraint030  label="SameOrientation013"  # WARN: FeaturePython — macro-defined, semantics opaque (R4)
  Disabled = false
  Group = -> [ElementLink059,ElementLink060]
  _ConstraintType = 2
  _Parent = -> Constraints
FEATURE [App::FeaturePython] ElementLink059  label="_Element048"  # link proxy (typed FeaturePython)
  LinkTransform = true
  LinkedObject = -> _Element048
  _Parent = -> Constraint030
FEATURE [Part::FeaturePython] _Element048  # link proxy (typed FeaturePython)
  Detach = false
  LinkTransform = true
  LinkedObject = -> Clone001 [Face16]
  _Parent = -> Elements
FEATURE [App::FeaturePython] ElementLink060  label="_Element042"  # link proxy (typed FeaturePython)
  LinkTransform = true
  LinkedObject = -> _Element042
  _Parent = -> Constraint030
FEATURE [App::FeaturePython] Constraint031  label="MidPoint014"  # WARN: FeaturePython — macro-defined, semantics opaque (R4)
  Disabled = false
  Group = -> [ElementLink061,ElementLink062]
  _ConstraintType = 20
  _Parent = -> Constraints
FEATURE [App::FeaturePython] ElementLink061  label="_Element049"  # link proxy (typed FeaturePython)
  LinkTransform = true
  LinkedObject = -> _Element049
  _Parent = -> Constraint031
FEATURE [Part::FeaturePython] _Element049  # link proxy (typed FeaturePython)
  Detach = false
  LinkTransform = true
  LinkedObject = -> Clone002 [Edge55]
  _Parent = -> Elements
FEATURE [App::FeaturePython] ElementLink062  label="_Element050"  # link proxy (typed FeaturePython)
  LinkTransform = true
  LinkedObject = -> _Element050
  _Parent = -> Constraint031
FEATURE [Part::FeaturePython] _Element050  # link proxy (typed FeaturePython)
  Detach = false
  LinkTransform = true
  LinkedObject = -> Clone003 [Edge47]
  _Parent = -> Elements
FEATURE [App::FeaturePython] Constraint032  label="SameOrientation014"  # WARN: FeaturePython — macro-defined, semantics opaque (R4)
  Disabled = false
  Group = -> [ElementLink063,ElementLink064]
  _ConstraintType = 2
  _Parent = -> Constraints
FEATURE [App::FeaturePython] ElementLink063  label="_Element032"  # link proxy (typed FeaturePython)
  LinkTransform = true
  LinkedObject = -> _Element032
  _Parent = -> Constraint032
FEATURE [App::FeaturePython] ElementLink064  label="_Element051"  # link proxy (typed FeaturePython)
  LinkTransform = true
  LinkedObject = -> _Element051
  _Parent = -> Constraint032
FEATURE [Part::FeaturePython] _Element051  # link proxy (typed FeaturePython)
  Detach = false
  LinkTransform = true
  LinkedObject = -> Clone002 [Face21]
  _Parent = -> Elements
FEATURE [App::FeaturePython] Constraint033  label="MidPoint015"  # WARN: FeaturePython — macro-defined, semantics opaque (R4)
  Disabled = false
  Group = -> [ElementLink065,ElementLink066]
  _ConstraintType = 20
  _Parent = -> Constraints
FEATURE [App::FeaturePython] ElementLink065  label="_Element052"  # link proxy (typed FeaturePython)
  LinkTransform = true
  LinkedObject = -> _Element052
  _Parent = -> Constraint033
FEATURE [Part::FeaturePython] _Element052  # link proxy (typed FeaturePython)
  Detach = false
  LinkTransform = true
  LinkedObject = -> Link009 [Edge12]
  _Parent = -> Elements
FEATURE [App::FeaturePython] ElementLink066  label="_Element053"  # link proxy (typed FeaturePython)
  LinkTransform = true
  LinkedObject = -> _Element053
  _Parent = -> Constraint033
FEATURE [Part::FeaturePython] _Element053  # link proxy (typed FeaturePython)
  Detach = false
  LinkTransform = true
  LinkedObject = -> Clone002 [Edge59]
  _Parent = -> Elements
FEATURE [App::FeaturePython] Constraint034  label="SameOrientation015"  # WARN: FeaturePython — macro-defined, semantics opaque (R4)
  Disabled = false
  Group = -> [ElementLink067,ElementLink068]
  _ConstraintType = 2
  _Parent = -> Constraints
FEATURE [App::FeaturePython] ElementLink067  label="_Element054"  # link proxy (typed FeaturePython)
  LinkTransform = true
  LinkedObject = -> _Element054
  _Parent = -> Constraint034
FEATURE [Part::FeaturePython] _Element054  # link proxy (typed FeaturePython)
  Detach = false
  LinkTransform = true
  LinkedObject = -> Clone002 [Face16]
  _Parent = -> Elements
FEATURE [App::FeaturePython] ElementLink068  label="_Element055"  # link proxy (typed FeaturePython)
  LinkTransform = true
  LinkedObject = -> _Element055
  _Parent = -> Constraint034
FEATURE [Part::FeaturePython] _Element055  # link proxy (typed FeaturePython)
  Detach = false
  LinkTransform = true
  LinkedObject = -> Link009 [Face4]
  _Parent = -> Elements
FEATURE [App::FeaturePython] Constraint035  label="MidPoint016"  # WARN: FeaturePython — macro-defined, semantics opaque (R4)
  Disabled = false
  Group = -> [ElementLink069,ElementLink070]
  _ConstraintType = 20
  _Parent = -> Constraints
FEATURE [App::FeaturePython] ElementLink069  label="_Element056"  # link proxy (typed FeaturePython)
  LinkTransform = true
  LinkedObject = -> _Element056
  _Parent = -> Constraint035
FEATURE [Part::FeaturePython] _Element056  # link proxy (typed FeaturePython)
  Detach = false
  LinkTransform = true
  LinkedObject = -> Link010 [Edge24]
  _Parent = -> Elements
FEATURE [App::FeaturePython] ElementLink070  label="_Element057"  # link proxy (typed FeaturePython)
  LinkTransform = true
  LinkedObject = -> _Element057
  _Parent = -> Constraint035
FEATURE [Part::FeaturePython] _Element057  # link proxy (typed FeaturePython)
  Detach = false
  LinkTransform = true
  LinkedObject = -> SquarePipe_SS001 [Edge13]
  _Parent = -> Elements
FEATURE [App::FeaturePython] Constraint036  label="SameOrientation016"  # WARN: FeaturePython — macro-defined, semantics opaque (R4)
  Disabled = false
  Group = -> [ElementLink071,ElementLink072]
  _ConstraintType = 2
  _Parent = -> Constraints
FEATURE [App::FeaturePython] ElementLink071  label="_Element058"  # link proxy (typed FeaturePython)
  LinkTransform = true
  LinkedObject = -> _Element058
  _Parent = -> Constraint036
FEATURE [Part::FeaturePython] _Element058  # link proxy (typed FeaturePython)
  Detach = false
  LinkTransform = true
  LinkedObject = -> Link010 [Face8]
  _Parent = -> Elements
FEATURE [App::FeaturePython] ElementLink072  label="_Element059"  # link proxy (typed FeaturePython)
  LinkTransform = true
  LinkedObject = -> _Element059
  _Parent = -> Constraint036
FEATURE [Part::FeaturePython] _Element059  # link proxy (typed FeaturePython)
  Detach = false
  LinkTransform = true
  LinkedObject = -> SquarePipe_SS001 [Face18]
  _Parent = -> Elements
FEATURE [App::FeaturePython] Constraint037  label="MidPoint017"  # WARN: FeaturePython — macro-defined, semantics opaque (R4)
  Disabled = false
  Group = -> [ElementLink073,ElementLink074]
  _ConstraintType = 20
  _Parent = -> Constraints
FEATURE [App::FeaturePython] ElementLink073  label="_Element060"  # link proxy (typed FeaturePython)
  LinkTransform = true
  LinkedObject = -> _Element060
  _Parent = -> Constraint037
FEATURE [Part::FeaturePython] _Element060  # link proxy (typed FeaturePython)
  Detach = false
  LinkTransform = true
  LinkedObject = -> Link011 [Edge24]
  _Parent = -> Elements
FEATURE [App::FeaturePython] ElementLink074  label="_Element061"  # link proxy (typed FeaturePython)
  LinkTransform = true
  LinkedObject = -> _Element061
  _Parent = -> Constraint037
FEATURE [Part::FeaturePython] _Element061  # link proxy (typed FeaturePython)
  Detach = false
  LinkTransform = true
  LinkedObject = -> SquarePipe_SS001 [Edge7]
  _Parent = -> Elements
FEATURE [App::FeaturePython] Constraint038  label="SameOrientation017"  # WARN: FeaturePython — macro-defined, semantics opaque (R4)
  Disabled = false
  Group = -> [ElementLink075,ElementLink076]
  _ConstraintType = 2
  _Parent = -> Constraints
FEATURE [App::FeaturePython] ElementLink075  label="_Element062"  # link proxy (typed FeaturePython)
  LinkTransform = true
  LinkedObject = -> _Element062
  _Parent = -> Constraint038
FEATURE [Part::FeaturePython] _Element062  # link proxy (typed FeaturePython)
  Detach = false
  LinkTransform = true
  LinkedObject = -> Link011 [Face8]
  _Parent = -> Elements
FEATURE [App::FeaturePython] ElementLink076  label="_Element059"  # link proxy (typed FeaturePython)
  LinkTransform = true
  LinkedObject = -> _Element059
  _Parent = -> Constraint038
FEATURE [App::FeaturePython] Constraint039  label="MidPoint018"  # WARN: FeaturePython — macro-defined, semantics opaque (R4)
  Disabled = false
  Group = -> [ElementLink077,ElementLink078]
  _ConstraintType = 20
  _Parent = -> Constraints
FEATURE [App::FeaturePython] ElementLink077  label="_Element063"  # link proxy (typed FeaturePython)
  LinkTransform = true
  LinkedObject = -> _Element063
  _Parent = -> Constraint039
FEATURE [Part::FeaturePython] _Element063  # link proxy (typed FeaturePython)
  Detach = false
  LinkTransform = true
  LinkedObject = -> Clone005 [Edge47]
  _Parent = -> Elements
FEATURE [App::FeaturePython] ElementLink078  label="_Element064"  # link proxy (typed FeaturePython)
  LinkTransform = true
  LinkedObject = -> _Element064
  _Parent = -> Constraint039
FEATURE [Part::FeaturePython] _Element064  # link proxy (typed FeaturePython)
  Detach = false
  LinkTransform = true
  LinkedObject = -> Link006 [Edge13]
  _Parent = -> Elements
FEATURE [App::FeaturePython] Constraint040  label="SameOrientation018"  # WARN: FeaturePython — macro-defined, semantics opaque (R4)
  Disabled = false
  Group = -> [ElementLink079,ElementLink080]
  _ConstraintType = 2
  _Parent = -> Constraints
FEATURE [App::FeaturePython] ElementLink079  label="_Element065"  # link proxy (typed FeaturePython)
  LinkTransform = true
  LinkedObject = -> _Element065
  _Parent = -> Constraint040
FEATURE [Part::FeaturePython] _Element065  # link proxy (typed FeaturePython)
  Detach = false
  LinkTransform = true
  LinkedObject = -> Clone005 [Face16]
  _Parent = -> Elements
FEATURE [App::FeaturePython] ElementLink080  label="_Element066"  # link proxy (typed FeaturePython)
  LinkTransform = true
  LinkedObject = -> _Element066
  _Parent = -> Constraint040
FEATURE [Part::FeaturePython] _Element066  # link proxy (typed FeaturePython)
  Detach = false
  LinkTransform = true
  LinkedObject = -> Link006 [Face18]
  _Parent = -> Elements
FEATURE [App::FeaturePython] Constraint041  label="MidPoint019"  # WARN: FeaturePython — macro-defined, semantics opaque (R4)
  Disabled = false
  Group = -> [ElementLink081,ElementLink082]
  _ConstraintType = 20
  _Parent = -> Constraints
FEATURE [App::FeaturePython] ElementLink081  label="_Element067"  # link proxy (typed FeaturePython)
  LinkTransform = true
  LinkedObject = -> _Element067
  _Parent = -> Constraint041
FEATURE [Part::FeaturePython] _Element067  # link proxy (typed FeaturePython)
  Detach = false
  LinkTransform = true
  LinkedObject = -> Clone006 [Edge24]
  _Parent = -> Elements
FEATURE [App::FeaturePython] ElementLink082  label="_Element068"  # link proxy (typed FeaturePython)
  LinkTransform = true
  LinkedObject = -> _Element068
  _Parent = -> Constraint041
FEATURE [Part::FeaturePython] _Element068  # link proxy (typed FeaturePython)
  Detach = false
  LinkTransform = true
  LinkedObject = -> Link006 [Edge7]
  _Parent = -> Elements
FEATURE [App::FeaturePython] Constraint042  label="SameOrientation019"  # WARN: FeaturePython — macro-defined, semantics opaque (R4)
  Disabled = false
  Group = -> [ElementLink083,ElementLink084]
  _ConstraintType = 2
  _Parent = -> Constraints
FEATURE [App::FeaturePython] ElementLink083  label="_Element069"  # link proxy (typed FeaturePython)
  LinkTransform = true
  LinkedObject = -> _Element069
  _Parent = -> Constraint042
FEATURE [Part::FeaturePython] _Element069  # link proxy (typed FeaturePython)
  Detach = false
  LinkTransform = true
  LinkedObject = -> Clone006 [Face8]
  _Parent = -> Elements
FEATURE [App::FeaturePython] ElementLink084  label="_Element066"  # link proxy (typed FeaturePython)
  LinkTransform = true
  LinkedObject = -> _Element066
  _Parent = -> Constraint042
FEATURE [App::FeaturePython] Constraint043  label="MidPoint020"  # WARN: FeaturePython — macro-defined, semantics opaque (R4)
  Disabled = false
  Group = -> [ElementLink085,ElementLink086]
  _ConstraintType = 20
  _Parent = -> Constraints
FEATURE [App::FeaturePython] ElementLink085  label="_Element070"  # link proxy (typed FeaturePython)
  LinkTransform = true
  LinkedObject = -> _Element070
  _Parent = -> Constraint043
FEATURE [Part::FeaturePython] _Element070  # link proxy (typed FeaturePython)
  Detach = false
  LinkTransform = true
  LinkedObject = -> Clone007 [Edge24]
  _Parent = -> Elements
FEATURE [App::FeaturePython] ElementLink086  label="_Element071"  # link proxy (typed FeaturePython)
  LinkTransform = true
  LinkedObject = -> _Element071
  _Parent = -> Constraint043
FEATURE [Part::FeaturePython] _Element071  # link proxy (typed FeaturePython)
  Detach = false
  LinkTransform = true
  LinkedObject = -> Link008 [Edge7]
  _Parent = -> Elements
FEATURE [App::FeaturePython] Constraint044  label="SameOrientation020"  # WARN: FeaturePython — macro-defined, semantics opaque (R4)
  Disabled = false
  Group = -> [ElementLink087,ElementLink088]
  _ConstraintType = 2
  _Parent = -> Constraints
FEATURE [App::FeaturePython] ElementLink087  label="_Element072"  # link proxy (typed FeaturePython)
  LinkTransform = true
  LinkedObject = -> _Element072
  _Parent = -> Constraint044
FEATURE [Part::FeaturePython] _Element072  # link proxy (typed FeaturePython)
  Detach = false
  LinkTransform = true
  LinkedObject = -> Clone007 [Face8]
  _Parent = -> Elements
FEATURE [App::FeaturePython] ElementLink088  label="_Element073"  # link proxy (typed FeaturePython)
  LinkTransform = true
  LinkedObject = -> _Element073
  _Parent = -> Constraint044
FEATURE [Part::FeaturePython] _Element073  # link proxy (typed FeaturePython)
  Detach = false
  LinkTransform = true
  LinkedObject = -> Link008 [Face18]
  _Parent = -> Elements
FEATURE [App::FeaturePython] Constraint045  label="MidPoint021"  # WARN: FeaturePython — macro-defined, semantics opaque (R4)
  Disabled = false
  Group = -> [ElementLink089,ElementLink090]
  _ConstraintType = 20
  _Parent = -> Constraints
FEATURE [App::FeaturePython] ElementLink089  label="_Element074"  # link proxy (typed FeaturePython)
  LinkTransform = true
  LinkedObject = -> _Element074
  _Parent = -> Constraint045
FEATURE [Part::FeaturePython] _Element074  # link proxy (typed FeaturePython)
  Detach = false
  LinkTransform = true
  LinkedObject = -> Clone008 [Edge24]
  _Parent = -> Elements
FEATURE [App::FeaturePython] ElementLink090  label="_Element075"  # link proxy (typed FeaturePython)
  LinkTransform = true
  LinkedObject = -> _Element075
  _Parent = -> Constraint045
FEATURE [Part::FeaturePython] _Element075  # link proxy (typed FeaturePython)
  Detach = false
  LinkTransform = true
  LinkedObject = -> Link005 [Edge13]
  _Parent = -> Elements
FEATURE [App::FeaturePython] Constraint046  label="SameOrientation021"  # WARN: FeaturePython — macro-defined, semantics opaque (R4)
  Disabled = false
  Group = -> [ElementLink091,ElementLink092]
  _ConstraintType = 2
  _Parent = -> Constraints
FEATURE [App::FeaturePython] ElementLink091  label="_Element076"  # link proxy (typed FeaturePython)
  LinkTransform = true
  LinkedObject = -> _Element076
  _Parent = -> Constraint046
FEATURE [Part::FeaturePython] _Element076  # link proxy (typed FeaturePython)
  Detach = false
  LinkTransform = true
  LinkedObject = -> Clone008 [Face8]
  _Parent = -> Elements
FEATURE [App::FeaturePython] ElementLink092  label="_Element077"  # link proxy (typed FeaturePython)
  LinkTransform = true
  LinkedObject = -> _Element077
  _Parent = -> Constraint046
FEATURE [Part::FeaturePython] _Element077  # link proxy (typed FeaturePython)
  Detach = false
  LinkTransform = true
  LinkedObject = -> Link005 [Face18]
  _Parent = -> Elements
FEATURE [App::FeaturePython] Constraint047  label="MidPoint022"  # WARN: FeaturePython — macro-defined, semantics opaque (R4)
  Disabled = false
  Group = -> [ElementLink093,ElementLink094]
  _ConstraintType = 20
  _Parent = -> Constraints
FEATURE [App::FeaturePython] ElementLink093  label="_Element078"  # link proxy (typed FeaturePython)
  LinkTransform = true
  LinkedObject = -> _Element078
  _Parent = -> Constraint047
FEATURE [Part::FeaturePython] _Element078  # link proxy (typed FeaturePython)
  Detach = false
  LinkTransform = true
  LinkedObject = -> Clone009 [Edge47]
  _Parent = -> Elements
FEATURE [App::FeaturePython] ElementLink094  label="_Element079"  # link proxy (typed FeaturePython)
  LinkTransform = true
  LinkedObject = -> _Element079
  _Parent = -> Constraint047
FEATURE [Part::FeaturePython] _Element079  # link proxy (typed FeaturePython)
  Detach = false
  LinkTransform = true
  LinkedObject = -> Link007 [Edge13]
  _Parent = -> Elements
FEATURE [App::FeaturePython] Constraint048  label="SameOrientation022"  # WARN: FeaturePython — macro-defined, semantics opaque (R4)
  Disabled = false
  Group = -> [ElementLink095,ElementLink096]
  _ConstraintType = 2
  _Parent = -> Constraints
FEATURE [App::FeaturePython] ElementLink095  label="_Element080"  # link proxy (typed FeaturePython)
  LinkTransform = true
  LinkedObject = -> _Element080
  _Parent = -> Constraint048
FEATURE [Part::FeaturePython] _Element080  # link proxy (typed FeaturePython)
  Detach = false
  LinkTransform = true
  LinkedObject = -> Clone009 [Face16]
  _Parent = -> Elements
FEATURE [App::FeaturePython] ElementLink096  label="_Element081"  # link proxy (typed FeaturePython)
  LinkTransform = true
  LinkedObject = -> _Element081
  _Parent = -> Constraint048
FEATURE [Part::FeaturePython] _Element081  # link proxy (typed FeaturePython)
  Detach = false
  LinkTransform = true
  LinkedObject = -> Link007 [Face18]
  _Parent = -> Elements
FEATURE [App::FeaturePython] Constraint049  label="MidPoint023"  # WARN: FeaturePython — macro-defined, semantics opaque (R4)
  Disabled = false
  Group = -> [ElementLink097,ElementLink098]
  _ConstraintType = 20
  _Parent = -> Constraints
FEATURE [App::FeaturePython] ElementLink097  label="_Element082"  # link proxy (typed FeaturePython)
  LinkTransform = true
  LinkedObject = -> _Element082
  _Parent = -> Constraint049
FEATURE [Part::FeaturePython] _Element082  # link proxy (typed FeaturePython)
  Detach = false
  LinkTransform = true
  LinkedObject = -> Link003 [Edge47]
  _Parent = -> Elements
FEATURE [App::FeaturePython] ElementLink098  label="_Element037"  # link proxy (typed FeaturePython)
  LinkTransform = true
  LinkedObject = -> _Element037
  _Parent = -> Constraint049
FEATURE [App::FeaturePython] Constraint050  label="SameOrientation023"  # WARN: FeaturePython — macro-defined, semantics opaque (R4)
  Disabled = false
  Group = -> [ElementLink099,ElementLink100]
  _ConstraintType = 2
  _Parent = -> Constraints
FEATURE [App::FeaturePython] ElementLink099  label="_Element083"  # link proxy (typed FeaturePython)
  LinkTransform = true
  LinkedObject = -> _Element083
  _Parent = -> Constraint050
FEATURE [Part::FeaturePython] _Element083  # link proxy (typed FeaturePython)
  Detach = false
  LinkTransform = true
  LinkedObject = -> Link003 [Face16]
  _Parent = -> Elements
FEATURE [App::FeaturePython] ElementLink100  label="_Element035"  # link proxy (typed FeaturePython)
  LinkTransform = true
  LinkedObject = -> _Element035
  _Parent = -> Constraint050
FEATURE [App::FeaturePython] Constraint051  label="MidPoint024"  # WARN: FeaturePython — macro-defined, semantics opaque (R4)
  Disabled = false
  Group = -> [ElementLink101,ElementLink102]
  _ConstraintType = 20
  _Parent = -> Constraints
FEATURE [App::FeaturePython] ElementLink101  label="_Element084"  # link proxy (typed FeaturePython)
  LinkTransform = true
  LinkedObject = -> _Element084
  _Parent = -> Constraint051
FEATURE [Part::FeaturePython] _Element084  # link proxy (typed FeaturePython)
  Detach = false
  LinkTransform = true
  LinkedObject = -> H200x100x5_5_011 [Edge47]
  _Parent = -> Elements
FEATURE [App::FeaturePython] ElementLink102  label="_Element085"  # link proxy (typed FeaturePython)
  LinkTransform = true
  LinkedObject = -> _Element085
  _Parent = -> Constraint051
FEATURE [Part::FeaturePython] _Element085  # link proxy (typed FeaturePython)
  Detach = false
  LinkTransform = true
  LinkedObject = -> Link003 [Edge1]
  _Parent = -> Elements
FEATURE [App::FeaturePython] Constraint052  label="SameOrientation024"  # WARN: FeaturePython — macro-defined, semantics opaque (R4)
  Disabled = false
  Group = -> [ElementLink103,ElementLink104]
  _ConstraintType = 2
  _Parent = -> Constraints
FEATURE [App::FeaturePython] ElementLink103  label="_Element086"  # link proxy (typed FeaturePython)
  LinkTransform = true
  LinkedObject = -> _Element086
  _Parent = -> Constraint052
FEATURE [Part::FeaturePython] _Element086  # link proxy (typed FeaturePython)
  Detach = false
  LinkTransform = true
  LinkedObject = -> H200x100x5_5_011 [Face16]
  _Parent = -> Elements
FEATURE [App::FeaturePython] ElementLink104  label="_Element083"  # link proxy (typed FeaturePython)
  LinkTransform = true
  LinkedObject = -> _Element083
  _Parent = -> Constraint052
FEATURE [App::FeaturePython] Constraint053  label="MidPoint025"  # WARN: FeaturePython — macro-defined, semantics opaque (R4)
  Disabled = false
  Group = -> [ElementLink105,ElementLink106]
  _ConstraintType = 20
  _Parent = -> Constraints
FEATURE [App::FeaturePython] ElementLink105  label="_Element087"  # link proxy (typed FeaturePython)
  LinkTransform = true
  LinkedObject = -> _Element087
  _Parent = -> Constraint053
FEATURE [Part::FeaturePython] _Element087  # link proxy (typed FeaturePython)
  Detach = false
  LinkTransform = true
  LinkedObject = -> Clone004 [Edge47]
  _Parent = -> Elements
FEATURE [App::FeaturePython] ElementLink106  label="_Element088"  # link proxy (typed FeaturePython)
  LinkTransform = true
  LinkedObject = -> _Element088
  _Parent = -> Constraint053
FEATURE [Part::FeaturePython] _Element088  # link proxy (typed FeaturePython)
  Detach = false
  LinkTransform = true
  LinkedObject = -> Clone001 [Edge1]
  _Parent = -> Elements
FEATURE [App::FeaturePython] Constraint054  label="SameOrientation025"  # WARN: FeaturePython — macro-defined, semantics opaque (R4)
  Disabled = false
  Group = -> [ElementLink107,ElementLink108]
  _ConstraintType = 2
  _Parent = -> Constraints
FEATURE [App::FeaturePython] ElementLink107  label="_Element089"  # link proxy (typed FeaturePython)
  LinkTransform = true
  LinkedObject = -> _Element089
  _Parent = -> Constraint054
FEATURE [Part::FeaturePython] _Element089  # link proxy (typed FeaturePython)
  Detach = false
  LinkTransform = true
  LinkedObject = -> Clone004 [Face16]
  _Parent = -> Elements
FEATURE [App::FeaturePython] ElementLink108  label="_Element048"  # link proxy (typed FeaturePython)
  LinkTransform = true
  LinkedObject = -> _Element048
  _Parent = -> Constraint054
FEATURE [Part::FeaturePython] _Element090  # link proxy (typed FeaturePython)
  Detach = false
  LinkTransform = true
  LinkedObject = -> C150x75x007 [Edge35]
  _Parent = -> Elements
FEATURE [Part::FeaturePython] _Element091  # link proxy (typed FeaturePython)
  Detach = false
  LinkTransform = true
  LinkedObject = -> Clone [Edge44]
  _Parent = -> Elements
FEATURE [App::FeaturePython] Constraint055  label="PointDistance"  # WARN: FeaturePython — macro-defined, semantics opaque (R4)
  Disabled = false
  Distance = 1000
  Group = -> [ElementLink109,ElementLink110]
  _ConstraintType = 5
  _Parent = -> Constraints
FEATURE [App::FeaturePython] ElementLink109  label="_Element092"  # link proxy (typed FeaturePython)
  LinkTransform = true
  LinkedObject = -> _Element092
  _Parent = -> Constraint055
FEATURE [Part::FeaturePython] _Element092  # link proxy (typed FeaturePython)
  Detach = false
  LinkTransform = true
  LinkedObject = -> C150x75x007 [Vertex2]
  _Parent = -> Elements
FEATURE [App::FeaturePython] ElementLink110  label="_Element093"  # link proxy (typed FeaturePython)
  LinkTransform = true
  LinkedObject = -> _Element093
  _Parent = -> Constraint055
FEATURE [Part::FeaturePython] _Element093  # link proxy (typed FeaturePython)
  Detach = false
  LinkTransform = true
  LinkedObject = -> H200x100x5_5_010 [Edge44]
  _Parent = -> Elements
FEATURE [App::FeaturePython] Constraint056  label="SameOrientation026"  # WARN: FeaturePython — macro-defined, semantics opaque (R4)
  Disabled = false
  Group = -> [ElementLink111,ElementLink112]
  _ConstraintType = 2
  _Parent = -> Constraints
FEATURE [App::FeaturePython] ElementLink111  label="_Element094"  # link proxy (typed FeaturePython)
  LinkTransform = true
  LinkedObject = -> _Element094
  _Parent = -> Constraint056
FEATURE [Part::FeaturePython] _Element094  # link proxy (typed FeaturePython)
  Detach = false
  LinkTransform = true
  LinkedObject = -> C150x75x007 [Face12]
  _Parent = -> Elements
FEATURE [App::FeaturePython] ElementLink112  label="_Element029"  # link proxy (typed FeaturePython)
  LinkTransform = true
  LinkedObject = -> _Element029
  _Parent = -> Constraint056
FEATURE [App::FeaturePython] Constraint057  label="AxialAlignment"  # WARN: FeaturePython — macro-defined, semantics opaque (R4)
  Angle = 0
  AnglePitch = 0
  AngleRoll = 0
  Disabled = false
  Group = -> [ElementLink113,ElementLink114]
  LockAngle = false
  Multiply = false
  _ConstraintType = 36
  _Parent = -> Constraints
FEATURE [App::FeaturePython] ElementLink113  label="_Element090"  # link proxy (typed FeaturePython)
  LinkTransform = true
  LinkedObject = -> _Element090
  _Parent = -> Constraint057
FEATURE [App::FeaturePython] ElementLink114  label="_Element091"  # link proxy (typed FeaturePython)
  LinkTransform = true
  LinkedObject = -> _Element091
  _Parent = -> Constraint057
FEATURE [App::FeaturePython] Constraint058  label="AxialAlignment001"  # WARN: FeaturePython — macro-defined, semantics opaque (R4)
  Angle = 0
  AnglePitch = 0
  AngleRoll = 0
  Disabled = false
  Group = -> [ElementLink115,ElementLink116]
  LockAngle = false
  Multiply = false
  _ConstraintType = 36
  _Parent = -> Constraints
FEATURE [App::FeaturePython] ElementLink115  label="_Element095"  # link proxy (typed FeaturePython)
  LinkTransform = true
  LinkedObject = -> _Element095
  _Parent = -> Constraint058
FEATURE [Part::FeaturePython] _Element095  # link proxy (typed FeaturePython)
  Detach = false
  LinkTransform = true
  LinkedObject = -> C150x75x008 [Edge1]
  _Parent = -> Elements
FEATURE [App::FeaturePython] ElementLink116  label="_Element096"  # link proxy (typed FeaturePython)
  LinkTransform = true
  LinkedObject = -> _Element096
  _Parent = -> Constraint058
FEATURE [Part::FeaturePython] _Element096  # link proxy (typed FeaturePython)
  Detach = false
  LinkTransform = true
  LinkedObject = -> C150x75x007 [Edge1]
  _Parent = -> Elements
FEATURE [App::FeaturePython] Constraint059  label="SameOrientation027"  # WARN: FeaturePython — macro-defined, semantics opaque (R4)
  Disabled = false
  Group = -> [ElementLink117,ElementLink118]
  _ConstraintType = 2
  _Parent = -> Constraints
FEATURE [App::FeaturePython] ElementLink117  label="_Element097"  # link proxy (typed FeaturePython)
  LinkTransform = true
  LinkedObject = -> _Element097
  _Parent = -> Constraint059
FEATURE [Part::FeaturePython] _Element097  # link proxy (typed FeaturePython)
  Detach = false
  LinkTransform = true
  LinkedObject = -> C150x75x008 [Face12]
  _Parent = -> Elements
FEATURE [App::FeaturePython] ElementLink118  label="_Element026"  # link proxy (typed FeaturePython)
  LinkTransform = true
  LinkedObject = -> _Element026
  _Parent = -> Constraint059
